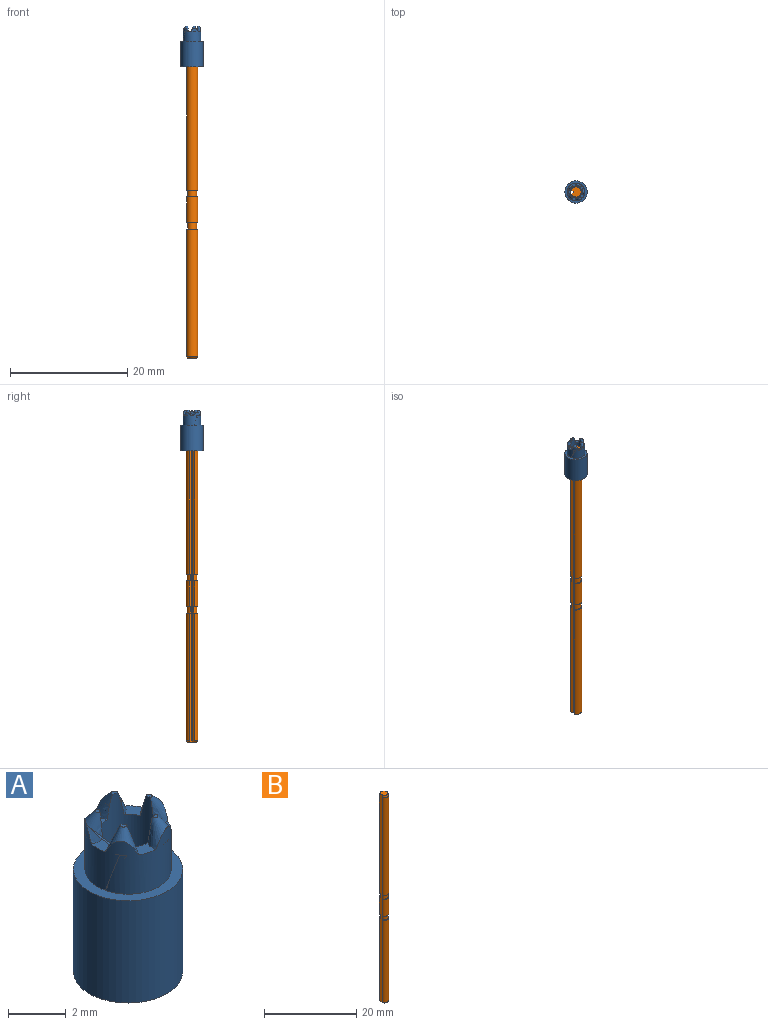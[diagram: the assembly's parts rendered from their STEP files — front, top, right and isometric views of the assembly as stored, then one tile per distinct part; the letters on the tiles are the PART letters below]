
ASSEMBLY  parts=2 mates=1
PART A: 30 faces, bbox 3.9x3.9x7.1 mm
  f0: plane 0.39x0.02mm, normal (0.34,0,-0.94), area 0mm2, adj f4,f5
  f1: cone r=0.6mm half-angle=24.8deg, axis (0.34,0,-0.94), area 1mm2, adj f2,f3,f4,f6,f26
  f2: plane 0.34x0.27mm, normal (0,0,1), area 0mm2, adj f1,f3
  f3: cylinder r=1mm len=6.95mm, axis (0,0,-1), area 39.8mm2, adj f1,f2,f6,f7,f9,f11,f12,f14
  f4: cylinder r=1.5mm len=3mm, axis (0,0,-1), area 17.9mm2, adj f0,f1,f5,f6,f8,f9,f10,f11
  f5: plane 0.38x0.01mm, normal (0,0,1), area 0mm2, adj f0,f4
  f6: plane 0.83x0.8mm, normal (0,0,1), area 0.3mm2, adj f1,f3,f4,f9
  f7: plane 0.34x0.3mm, normal (0,0,1), area 0mm2, adj f3,f9
  f8: plane 0.37x0.13mm, normal (0.11,0.33,-0.94), area 0mm2, adj f4,f10
  f9: cone r=0.6mm half-angle=24.8deg, axis (0.11,0.33,-0.94), area 1mm2, adj f3,f4,f6,f7,f11
  f10: plane 0.37x0.12mm, normal (0,0,1), area 0mm2, adj f4,f8
  f11: plane 0.78x0.7mm, normal (0,0,1), area 0.3mm2, adj f3,f4,f9,f14
  f12: plane 0.34x0.32mm, normal (0,0,1), area 0mm2, adj f3,f14
  f13: plane 0.32x0.23mm, normal (-0.28,0.2,-0.94), area 0mm2, adj f4,f15
  f14: cone r=0.6mm half-angle=24.8deg, axis (-0.28,0.2,-0.94), area 1mm2, adj f3,f4,f11,f12,f16
  f15: plane 0.31x0.23mm, normal (0,0,1), area 0mm2, adj f4,f13
  f16: plane 0.71x0.57mm, normal (0,0,1), area 0.3mm2, adj f3,f4,f14,f19
  f17: plane 0.34x0.32mm, normal (0,0,1), area 0mm2, adj f3,f19
  f18: plane 0.32x0.23mm, normal (-0.28,-0.2,-0.94), area 0mm2, adj f4,f20
  f19: cone r=0.6mm half-angle=24.8deg, axis (-0.28,-0.2,-0.94), area 1mm2, adj f3,f4,f16,f17,f21
  f20: plane 0.31x0.23mm, normal (0,0,1), area 0mm2, adj f4,f18
  f21: plane 0.78x0.7mm, normal (0,0,1), area 0.3mm2, adj f3,f4,f19,f23
  f22: plane 0.37x0.13mm, normal (0.11,-0.33,-0.94), area 0mm2, adj f4,f25
  f23: cone r=0.6mm half-angle=24.8deg, axis (0.11,-0.33,-0.94), area 1mm2, adj f3,f4,f21,f24,f26
  f24: plane 0.34x0.3mm, normal (0,0,1), area 0mm2, adj f3,f23
  f25: plane 0.37x0.12mm, normal (0,0,1), area 0mm2, adj f4,f22
  f26: plane 0.83x0.8mm, normal (0,0,1), area 0.3mm2, adj f1,f3,f4,f23
  f27: cylinder r=1.9mm len=4.35mm, axis (0,0,1), area 51.9mm2, adj f28,f29
  f28: plane 3.8x3.8mm, normal (0,0,-1), area 8.2mm2, adj f3,f27
  f29: plane 3.8x3.8mm, normal (0,0,1), area 4.3mm2, adj f4,f27
PART B: 16 faces, bbox 1.9x2x55 mm
  f0: cylinder r=1mm len=4.4mm, axis (0,0,-1), area 23.3mm2, adj f3,f5,f11,f15
  f1: cylinder r=1mm len=21.8mm, axis (0,0,-1), area 115.2mm2, adj f3,f5,f8,f12
  f2: cylinder r=0.1mm len=55mm, axis (0,0,-1), area 8.6mm2, adj f3,f5,f6,f7
  f3: plane 55.01x0.42mm, normal (-0.71,0.71,0), area 31.2mm2, adj f0,f1,f2,f4,f6,f7,f8,f9
  f4: cylinder r=1mm len=25.9mm, axis (0,0,-1), area 136.9mm2, adj f3,f5,f9,f14
  f5: plane 55.01x0.42mm, normal (-0.71,-0.71,0), area 31.2mm2, adj f0,f1,f2,f4,f6,f7,f8,f9
  f6: plane 1.73x1.65mm, normal (0,0,1), area 2.2mm2, adj f2,f3,f5,f9
  f7: plane 1.6x1.53mm, normal (0,0,-1), area 1.9mm2, adj f2,f3,f5,f8
  f8: cone r=1mm half-angle=45deg, axis (0,0,1), area 1.4mm2, adj f1,f3,f5,f7
  f9: cone r=0.87mm half-angle=15deg, axis (0,0,-1), area 2.6mm2, adj f3,f4,f5,f6
  f10: cylinder r=0.8mm len=1.6mm, axis (0,0,-1), area 4.8mm2, adj f3,f5,f11,f12
  f11: plane 2x1.88mm, normal (0,0,-1), area 1mm2, adj f0,f3,f5,f10
  f12: plane 2x1.88mm, normal (0,0,1), area 1mm2, adj f1,f3,f5,f10
  f13: cylinder r=0.8mm len=1.6mm, axis (0,0,-1), area 4.8mm2, adj f3,f5,f14,f15
  f14: plane 2x1.88mm, normal (0,0,-1), area 1mm2, adj f3,f4,f5,f13
  f15: plane 2x1.88mm, normal (0,0,1), area 1mm2, adj f0,f3,f5,f13
PLACE A at identity fixed
PLACE B t=(0,0,-54.05)mm
MATE fastened B.f0 <-> A.f3  axis (0,0,1) through (0,0,0.95)mm
